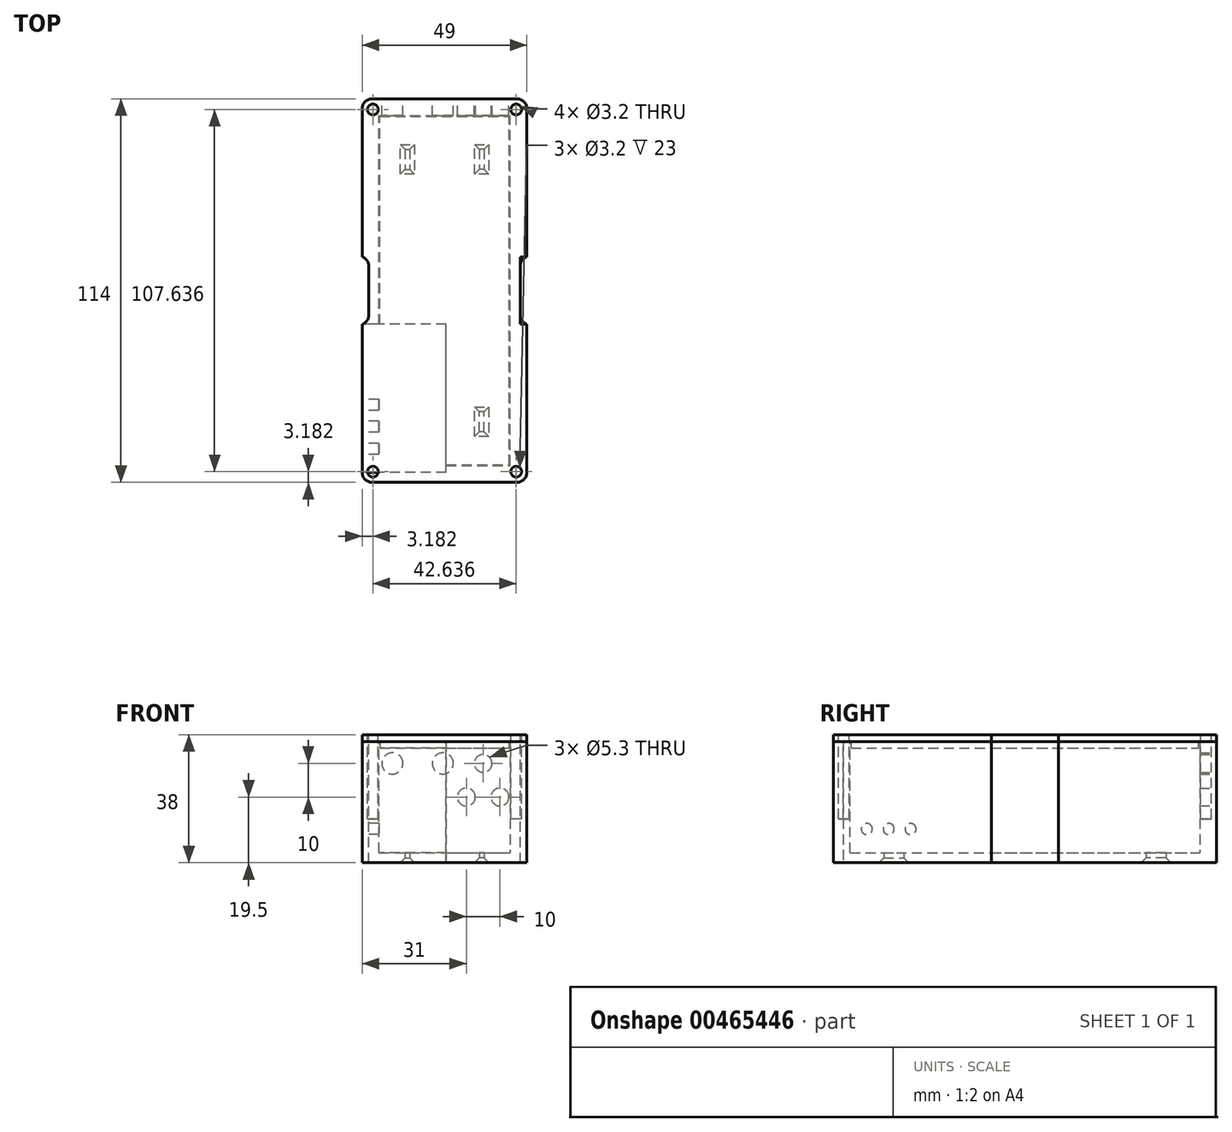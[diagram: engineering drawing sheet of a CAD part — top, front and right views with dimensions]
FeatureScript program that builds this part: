
annotation { "Feature Type Name" : "Feature", "Feature Type Description" : "" }
export const myFeature = defineFeature(function(context is Context, id is Id, definition is map)
    precondition{}
    {
        {
            var Q0;
            Q0=qCreatedBy(makeId("Top.planeOp"),FACE);
            var sketch = newSketch(context, id + "F0", { "sketchPlane" : qUnion([Q0])});
            skLineSegment(sketch, "E0.bottom", {"start": v(0, 0) * mm, "end": v(35, 0) * mm, "construction": true});
            skLineSegment(sketch, "E0.top", {"start": v(0, 100) * mm, "end": v(35, 100) * mm, "construction": true});
            skLineSegment(sketch, "E0.left", {"start": v(0, 0) * mm, "end": v(0, 100) * mm, "construction": true});
            skLineSegment(sketch, "E0.right", {"start": v(35, 0) * mm, "end": v(35, 100) * mm, "construction": true});
            skLineSegment(sketch, "E1.0", {"start": v(37, -2) * mm, "end": v(37, 102) * mm});
            skLineSegment(sketch, "E1.1", {"start": v(-2, -2) * mm, "end": v(37, -2) * mm});
            skLineSegment(sketch, "E1.2", {"start": v(-2, -2) * mm, "end": v(-2, 102) * mm});
            skLineSegment(sketch, "E1.3", {"start": v(-2, 102) * mm, "end": v(37, 102) * mm});
            skLineSegment(sketch, "E2.0", {"start": v(-7, 107) * mm, "end": v(42, 107) * mm});
            skLineSegment(sketch, "E2.1", {"start": v(-7, -7) * mm, "end": v(-7, 107) * mm});
            skLineSegment(sketch, "E2.2", {"start": v(-7, -7) * mm, "end": v(42, -7) * mm});
            skLineSegment(sketch, "E2.3", {"start": v(42, -7) * mm, "end": v(42, 107) * mm});
            skSolve(sketch);
        }
        {
            var Q0;
            Q0 = qSketchRegion(id + "F0", true);
            extrude(context, id + "F1", {"entities" : qUnion([Q0]), "depth" : 33 * mm});
        }
        {
            var Q0;
            Q0=makeQuery(id+"F1.opExtrude","CAP_FACE",FACE,{"disambiguationData":[OSD([sQuery(id+"F0.wireOp",EDGE,"E1.0"),sQuery(id+"F0.wireOp",EDGE,"E1.1"),sQuery(id+"F0.wireOp",EDGE,"E1.2"),sQuery(id+"F0.wireOp",EDGE,"E1.3"),sQuery(id+"F0.wireOp",EDGE,"E2.0"),sQuery(id+"F0.wireOp",EDGE,"E2.1"),sQuery(id+"F0.wireOp",EDGE,"E2.2"),sQuery(id+"F0.wireOp",EDGE,"E2.3")])],"isStart":true});
            var sketch = newSketch(context, id + "F2", { "sketchPlane" : qUnion([Q0])});
            skLineSegment(sketch, "E3.bottom", {"start": v(-7, 7) * mm, "end": v(42, 7) * mm});
            skLineSegment(sketch, "E3.top", {"start": v(-7, -107) * mm, "end": v(42, -107) * mm});
            skLineSegment(sketch, "E3.left", {"start": v(-7, 7) * mm, "end": v(-7, -107) * mm});
            skLineSegment(sketch, "E3.right", {"start": v(42, 7) * mm, "end": v(42, -107) * mm});
            skSolve(sketch);
        }
        {
            var Q0;
            Q0 = qSketchRegion(id + "F2", true);
            extrude(context, id + "F3", {"entities" : qUnion([Q0]), "operationType" : NewBodyOperationType.ADD, "depth" : 3 * mm});
        }
        {
            var Q0;
            Q0=makeQuery(id+"F1.opExtrude","CAP_FACE",FACE,{"disambiguationData":[OSD([sQuery(id+"F0.wireOp",EDGE,"E1.0"),sQuery(id+"F0.wireOp",EDGE,"E1.1"),sQuery(id+"F0.wireOp",EDGE,"E1.2"),sQuery(id+"F0.wireOp",EDGE,"E1.3"),sQuery(id+"F0.wireOp",EDGE,"E2.0"),sQuery(id+"F0.wireOp",EDGE,"E2.1"),sQuery(id+"F0.wireOp",EDGE,"E2.2"),sQuery(id+"F0.wireOp",EDGE,"E2.3")])],"isStart":false});
            var sketch = newSketch(context, id + "F4", { "sketchPlane" : qUnion([Q0])});
            skLineSegment(sketch, "E4.bottom", {"start": v(42, -7) * mm, "end": v(-7, -7) * mm});
            skLineSegment(sketch, "E4.top", {"start": v(42, 107) * mm, "end": v(-7, 107) * mm});
            skLineSegment(sketch, "E4.left", {"start": v(42, -7) * mm, "end": v(42, 107) * mm});
            skLineSegment(sketch, "E4.right", {"start": v(-7, -7) * mm, "end": v(-7, 107) * mm});
            skSolve(sketch);
        }
        {
            var Q0;
            Q0 = qSketchRegion(id + "F4", true);
            extrude(context, id + "F5", {"entities" : qUnion([Q0]), "depth" : 2 * mm});
        }
        {
            var Q0;
            Q0=makeQuery(id+"F5.opExtrude","CAP_FACE",FACE,{"disambiguationData":[OSD([sQuery(id+"F4.wireOp",EDGE,"E4.bottom"),sQuery(id+"F4.wireOp",EDGE,"E4.top"),sQuery(id+"F4.wireOp",EDGE,"E4.left"),sQuery(id+"F4.wireOp",EDGE,"E4.right")])],"isStart":true});
            var sketch = newSketch(context, id + "F6", { "sketchPlane" : qUnion([Q0])});
            skLineSegment(sketch, "E5.0", {"start": v(-2, 2) * mm, "end": v(37, 2) * mm, "construction": true});
            skLineSegment(sketch, "E6.0", {"start": v(37, 2) * mm, "end": v(37, -102) * mm, "construction": true});
            skLineSegment(sketch, "E7.0", {"start": v(-2, -102) * mm, "end": v(37, -102) * mm, "construction": true});
            skLineSegment(sketch, "E8.0", {"start": v(-2, 2) * mm, "end": v(-2, -102) * mm, "construction": true});
            skLineSegment(sketch, "E9.0", {"start": v(-1.7, 1.7) * mm, "end": v(36.7, 1.7) * mm});
            skLineSegment(sketch, "E9.1", {"start": v(-1.7, 1.7) * mm, "end": v(-1.7, -101.7) * mm});
            skLineSegment(sketch, "E9.2", {"start": v(-1.7, -101.7) * mm, "end": v(36.7, -101.7) * mm});
            skLineSegment(sketch, "E9.3", {"start": v(36.7, 1.7) * mm, "end": v(36.7, -101.7) * mm});
            skSolve(sketch);
        }
        {
            var Q0;
            Q0 = qSketchRegion(id + "F6", true);
            extrude(context, id + "F7", {"entities" : qUnion([Q0]), "operationType" : NewBodyOperationType.ADD, "depth" : 2 * mm});
        }
        {
            var Q0;
            Q0=makeQuery(id+"F5.opExtrude","CAP_FACE",FACE,{"disambiguationData":[OSD([sQuery(id+"F4.wireOp",EDGE,"E4.bottom"),sQuery(id+"F4.wireOp",EDGE,"E4.top"),sQuery(id+"F4.wireOp",EDGE,"E4.left"),sQuery(id+"F4.wireOp",EDGE,"E4.right")])],"isStart":false});
            var sketch = newSketch(context, id + "F8", { "sketchPlane" : qUnion([Q0])});
            skCircle(sketch, "E10", {"center": v(-3.82, -3.82) * mm, "radius": 1.3 * mm});
            skLineSegment(sketch, "E11", {"start": v(-2, -2) * mm, "end": v(-7, -7) * mm});
            skLineSegment(sketch, "E12", {"start": v(17.5, -7) * mm, "end": v(17.5, -36.45) * mm, "construction": true});
            skLineSegment(sketch, "E13", {"start": v(-7, 50) * mm, "end": v(-34.4, 50) * mm, "construction": true});
            skCircle(sketch, "E14.MirrorC", {"center": v(-3.82, 103.82) * mm, "radius": 1.3 * mm});
            skCircle(sketch, "E15.MirrorC", {"center": v(38.82, 103.82) * mm, "radius": 1.3 * mm});
            skCircle(sketch, "E16.MirrorC", {"center": v(38.82, -3.82) * mm, "radius": 1.3 * mm});
            skSolve(sketch);
        }
        {
            var Q0;
            Q0 = qSketchRegion(id + "F8", true);
            extrude(context, id + "F9", {"entities" : qUnion([Q0]), "operationType" : NewBodyOperationType.REMOVE, "oppositeDirection" : true, "depth" : 25 * mm});
        }
        {
            var Q0;
            Q0=makeQuery(id+"F5.opExtrude","CAP_FACE",FACE,{"disambiguationData":[OSD([sQuery(id+"F4.wireOp",EDGE,"E4.bottom"),sQuery(id+"F4.wireOp",EDGE,"E4.top"),sQuery(id+"F4.wireOp",EDGE,"E4.left"),sQuery(id+"F4.wireOp",EDGE,"E4.right")])],"isStart":false});
            var sketch = newSketch(context, id + "F10", { "sketchPlane" : qUnion([Q0])});
            skCircle(sketch, "E17", {"center": v(-3.82, -3.82) * mm, "radius": 1.6 * mm});
            skCircle(sketch, "E18.MirrorC", {"center": v(-3.82, 103.82) * mm, "radius": 1.6 * mm});
            skCircle(sketch, "E19.MirrorC", {"center": v(38.82, -3.82) * mm, "radius": 1.6 * mm});
            skCircle(sketch, "E20.MirrorC", {"center": v(38.82, 103.82) * mm, "radius": 1.6 * mm});
            skSolve(sketch);
        }
        {
            var Q0;
            Q0 = qSketchRegion(id + "F10", true);
            extrude(context, id + "F11", {"entities" : qUnion([Q0]), "operationType" : NewBodyOperationType.REMOVE, "oppositeDirection" : true, "depth" : 25 * mm});
        }
        {
            var Q0;
            Q0=makeQuery(id+"F8.imprint","IMPRINT",FACE,{"disambiguationData":[TD([[makeQuery(id+"F8.imprint","IMPRINT",EDGE,{"derivedFrom":sQuery(id+"F8.wireOp",EDGE,"E14.MirrorC")}),1.0]])]});
            var sketch = newSketch(context, id + "F12", { "sketchPlane" : qUnion([Q0])});
            skLineSegment(sketch, "E21.bottom", {"start": v(-7, 60) * mm, "end": v(-5, 60) * mm});
            skLineSegment(sketch, "E21.top", {"start": v(-7, 40) * mm, "end": v(-5, 40) * mm});
            skLineSegment(sketch, "E21.left", {"start": v(-7, 60) * mm, "end": v(-7, 40) * mm});
            skLineSegment(sketch, "E21.right", {"start": v(-5, 60) * mm, "end": v(-5, 40) * mm});
            skPoint(sketch, "E22", {"position": v(-7, 50) * mm});
            skLineSegment(sketch, "E23.MirrorCS", {"start": v(42, 60) * mm, "end": v(42, 40) * mm});
            skLineSegment(sketch, "E24.MirrorCS", {"start": v(42, 60) * mm, "end": v(40, 60) * mm});
            skLineSegment(sketch, "E25.MirrorCS", {"start": v(40, 60) * mm, "end": v(40, 40) * mm});
            skLineSegment(sketch, "E26.MirrorCS", {"start": v(42, 40) * mm, "end": v(40, 40) * mm});
            skSolve(sketch);
        }
        {
            var Q0;
            Q0 = qSketchRegion(id + "F12", true);
            extrude(context, id + "F13", {"entities" : qUnion([Q0]), "operationType" : NewBodyOperationType.REMOVE, "endBound" : BoundingType.THROUGH_ALL, "oppositeDirection" : true, "depth" : 25 * mm});
        }
        {
            var Q0;
            {var subQ0=sQuery(id+"F12.wireOp",EDGE,"E21.bottom");var subQ1=sQuery(id+"F12.wireOp",EDGE,"E21.right");Q0=makeQuery(id+"F13.boolean.opBoolean","COPY",EDGE,{"disambiguationData":[TD([makeQuery(id+"F3.opExtrude","CAP_FACE",FACE,{"disambiguationData":[OSD([sQuery(id+"F2.wireOp",EDGE,"E3.bottom"),sQuery(id+"F2.wireOp",EDGE,"E3.top"),sQuery(id+"F2.wireOp",EDGE,"E3.left"),sQuery(id+"F2.wireOp",EDGE,"E3.right")])],"isStart":false})])],"derivedFrom":makeQuery(id+"F13.opExtrude","SWEPT_EDGE",EDGE,{"disambiguationData":[OSD([subQ0,subQ1])]})});}
            var Q1;
            {var subQ0=sQuery(id+"F4.wireOp",EDGE,"E4.right");var subQ1=sQuery(id+"F4.wireOp",EDGE,"E4.left");var subQ2=sQuery(id+"F4.wireOp",EDGE,"E4.top");var subQ3=sQuery(id+"F4.wireOp",EDGE,"E4.bottom");var subQ4=sQuery(id+"F12.wireOp",EDGE,"E21.bottom");var subQ5=sQuery(id+"F12.wireOp",EDGE,"E21.right");Q1=makeQuery(id+"F13.boolean.opBoolean","COPY",EDGE,{"disambiguationData":[TD([makeQuery(id+"F5.opExtrude","CAP_FACE",FACE,{"disambiguationData":[OSD([subQ3,subQ2,subQ1,subQ0])],"isStart":true})])],"derivedFrom":makeQuery(id+"F13.opExtrude","SWEPT_EDGE",EDGE,{"disambiguationData":[OSD([subQ4,subQ5])]})});}
            var Q2;
            {var subQ0=sQuery(id+"F4.wireOp",EDGE,"E4.right");var subQ1=sQuery(id+"F4.wireOp",EDGE,"E4.left");var subQ2=sQuery(id+"F4.wireOp",EDGE,"E4.top");var subQ3=sQuery(id+"F4.wireOp",EDGE,"E4.bottom");var subQ4=sQuery(id+"F12.wireOp",EDGE,"E21.top");var subQ5=sQuery(id+"F12.wireOp",EDGE,"E21.right");Q2=makeQuery(id+"F13.boolean.opBoolean","COPY",EDGE,{"disambiguationData":[TD([makeQuery(id+"F5.opExtrude","CAP_FACE",FACE,{"disambiguationData":[OSD([subQ3,subQ2,subQ1,subQ0])],"isStart":true})])],"derivedFrom":makeQuery(id+"F13.opExtrude","SWEPT_EDGE",EDGE,{"disambiguationData":[OSD([subQ4,subQ5])]})});}
            var Q3;
            {var subQ0=sQuery(id+"F12.wireOp",EDGE,"E21.right");var subQ1=sQuery(id+"F12.wireOp",EDGE,"E21.top");Q3=makeQuery(id+"F13.boolean.opBoolean","COPY",EDGE,{"disambiguationData":[TD([makeQuery(id+"F3.opExtrude","CAP_FACE",FACE,{"disambiguationData":[OSD([sQuery(id+"F2.wireOp",EDGE,"E3.bottom"),sQuery(id+"F2.wireOp",EDGE,"E3.top"),sQuery(id+"F2.wireOp",EDGE,"E3.left"),sQuery(id+"F2.wireOp",EDGE,"E3.right")])],"isStart":false})])],"derivedFrom":makeQuery(id+"F13.opExtrude","SWEPT_EDGE",EDGE,{"disambiguationData":[OSD([subQ1,subQ0])]})});}
            var Q4;
            {var subQ0=sQuery(id+"F12.wireOp",EDGE,"E25.MirrorCS");var subQ1=sQuery(id+"F12.wireOp",EDGE,"E24.MirrorCS");Q4=makeQuery(id+"F13.boolean.opBoolean","COPY",EDGE,{"disambiguationData":[TD([makeQuery(id+"F3.opExtrude","CAP_FACE",FACE,{"disambiguationData":[OSD([sQuery(id+"F2.wireOp",EDGE,"E3.bottom"),sQuery(id+"F2.wireOp",EDGE,"E3.top"),sQuery(id+"F2.wireOp",EDGE,"E3.left"),sQuery(id+"F2.wireOp",EDGE,"E3.right")])],"isStart":false})])],"derivedFrom":makeQuery(id+"F13.opExtrude","SWEPT_EDGE",EDGE,{"disambiguationData":[OSD([subQ1,subQ0])]})});}
            var Q5;
            {var subQ0=sQuery(id+"F12.wireOp",EDGE,"E25.MirrorCS");var subQ1=sQuery(id+"F12.wireOp",EDGE,"E26.MirrorCS");Q5=makeQuery(id+"F13.boolean.opBoolean","COPY",EDGE,{"disambiguationData":[TD([makeQuery(id+"F3.opExtrude","CAP_FACE",FACE,{"disambiguationData":[OSD([sQuery(id+"F2.wireOp",EDGE,"E3.bottom"),sQuery(id+"F2.wireOp",EDGE,"E3.top"),sQuery(id+"F2.wireOp",EDGE,"E3.left"),sQuery(id+"F2.wireOp",EDGE,"E3.right")])],"isStart":false})])],"derivedFrom":makeQuery(id+"F13.opExtrude","SWEPT_EDGE",EDGE,{"disambiguationData":[OSD([subQ0,subQ1])]})});}
            var Q6;
            Q6=makeQuery(id+"F3.boolean.opBoolean","MERGE",EDGE,{"derivedFrom":[makeQuery(id+"F1.opExtrude","SWEPT_EDGE",EDGE,{"disambiguationData":[OSD([sQuery(id+"F0.wireOp",EDGE,"E2.0"),sQuery(id+"F0.wireOp",EDGE,"E2.1")])]}),makeQuery(id+"F3.opExtrude","SWEPT_EDGE",EDGE,{"disambiguationData":[OSD([sQuery(id+"F2.wireOp",EDGE,"E3.top"),sQuery(id+"F2.wireOp",EDGE,"E3.left")])]})]});
            var Q7;
            Q7=makeQuery(id+"F3.boolean.opBoolean","MERGE",EDGE,{"derivedFrom":[makeQuery(id+"F1.opExtrude","SWEPT_EDGE",EDGE,{"disambiguationData":[OSD([sQuery(id+"F0.wireOp",EDGE,"E2.0"),sQuery(id+"F0.wireOp",EDGE,"E2.3")])]}),makeQuery(id+"F3.opExtrude","SWEPT_EDGE",EDGE,{"disambiguationData":[OSD([sQuery(id+"F2.wireOp",EDGE,"E3.top"),sQuery(id+"F2.wireOp",EDGE,"E3.right")])]})]});
            var Q8;
            Q8=makeQuery(id+"F5.opExtrude","SWEPT_EDGE",EDGE,{"disambiguationData":[OSD([sQuery(id+"F4.wireOp",EDGE,"E4.top"),sQuery(id+"F4.wireOp",EDGE,"E4.left")])]});
            var Q9;
            Q9=makeQuery(id+"F5.opExtrude","SWEPT_EDGE",EDGE,{"disambiguationData":[OSD([sQuery(id+"F4.wireOp",EDGE,"E4.top"),sQuery(id+"F4.wireOp",EDGE,"E4.right")])]});
            var Q10;
            Q10=makeQuery(id+"F3.boolean.opBoolean","MERGE",EDGE,{"derivedFrom":[makeQuery(id+"F1.opExtrude","SWEPT_EDGE",EDGE,{"disambiguationData":[OSD([sQuery(id+"F0.wireOp",EDGE,"E2.1"),sQuery(id+"F0.wireOp",EDGE,"E2.2")])]}),makeQuery(id+"F3.opExtrude","SWEPT_EDGE",EDGE,{"disambiguationData":[OSD([sQuery(id+"F2.wireOp",EDGE,"E3.bottom"),sQuery(id+"F2.wireOp",EDGE,"E3.left")])]})]});
            var Q11;
            Q11=makeQuery(id+"F5.opExtrude","SWEPT_EDGE",EDGE,{"disambiguationData":[OSD([sQuery(id+"F4.wireOp",EDGE,"E4.bottom"),sQuery(id+"F4.wireOp",EDGE,"E4.right")])]});
            var Q12;
            Q12=makeQuery(id+"F5.opExtrude","SWEPT_EDGE",EDGE,{"disambiguationData":[OSD([sQuery(id+"F4.wireOp",EDGE,"E4.bottom"),sQuery(id+"F4.wireOp",EDGE,"E4.left")])]});
            var Q13;
            Q13=makeQuery(id+"F3.boolean.opBoolean","MERGE",EDGE,{"derivedFrom":[makeQuery(id+"F1.opExtrude","SWEPT_EDGE",EDGE,{"disambiguationData":[OSD([sQuery(id+"F0.wireOp",EDGE,"E2.2"),sQuery(id+"F0.wireOp",EDGE,"E2.3")])]}),makeQuery(id+"F3.opExtrude","SWEPT_EDGE",EDGE,{"disambiguationData":[OSD([sQuery(id+"F2.wireOp",EDGE,"E3.bottom"),sQuery(id+"F2.wireOp",EDGE,"E3.right")])]})]});
            fillet(context, id + "F14", {"entities" : qUnion([Q0, Q1, Q2, Q3, Q4, Q5, Q6, Q7, Q8, Q9, Q10, Q11, Q12, Q13]), "radius" : 3 * mm, "tangentPropagation" : true, "allowEdgeOverflow" : false});
        }
        {
            var Q0;
            Q0=makeQuery(id+"F3.boolean.opBoolean","MERGE",FACE,{"derivedFrom":[makeQuery(id+"F1.opExtrude","SWEPT_FACE",FACE,{"disambiguationData":[OSD([sQuery(id+"F0.wireOp",EDGE,"E2.0")])]}),makeQuery(id+"F3.opExtrude","SWEPT_FACE",FACE,{"disambiguationData":[OSD([sQuery(id+"F2.wireOp",EDGE,"E3.top")])]})]});
            var sketch = newSketch(context, id + "F15", { "sketchPlane" : qUnion([Q0])});
            skCircle(sketch, "E27", {"center": v(-17, 26.5) * mm, "radius": 3.15 * mm});
            skLineSegment(sketch, "E28", {"start": v(-2, 26.5) * mm, "end": v(-23.16, 26.5) * mm, "construction": true});
            skCircle(sketch, "E29", {"center": v(-2, 26.5) * mm, "radius": 3.15 * mm});
            skSolve(sketch);
        }
        {
            var Q0;
            Q0 = qSketchRegion(id + "F15", true);
            extrude(context, id + "F16", {"entities" : qUnion([Q0]), "operationType" : NewBodyOperationType.REMOVE, "oppositeDirection" : true, "depth" : 25 * mm});
        }
        {
            var Q0;
            Q0=makeQuery(id+"F3.opExtrude","CAP_FACE",FACE,{"disambiguationData":[OSD([sQuery(id+"F2.wireOp",EDGE,"E3.bottom"),sQuery(id+"F2.wireOp",EDGE,"E3.top"),sQuery(id+"F2.wireOp",EDGE,"E3.left"),sQuery(id+"F2.wireOp",EDGE,"E3.right")])],"isStart":false});
            var sketch = newSketch(context, id + "F17", { "sketchPlane" : qUnion([Q0])});
            skLineSegment(sketch, "E30.bottom", {"start": v(11.2, 21.25) * mm, "end": v(23.8, 21.25) * mm});
            skLineSegment(sketch, "E30.top", {"start": v(11.2, -119.18) * mm, "end": v(23.8, -119.18) * mm});
            skLineSegment(sketch, "E30.left", {"start": v(11.2, 21.25) * mm, "end": v(11.2, -119.18) * mm, "construction": true});
            skLineSegment(sketch, "E30.right", {"start": v(23.8, 21.25) * mm, "end": v(23.8, -119.18) * mm, "construction": true});
            skPoint(sketch, "E31", {"position": v(17.5, 21.25) * mm});
            skLineSegment(sketch, "E32.bottom", {"start": v(5.7, -8) * mm, "end": v(7.2, -8) * mm});
            skLineSegment(sketch, "E32.top", {"start": v(5.7, -14) * mm, "end": v(7.2, -14) * mm});
            skLineSegment(sketch, "E32.left", {"start": v(5.7, -8) * mm, "end": v(5.7, -14) * mm});
            skLineSegment(sketch, "E32.right", {"start": v(7.2, -8) * mm, "end": v(7.2, -14) * mm});
            skLineSegment(sketch, "E33.MirrorCS", {"start": v(29.3, -8) * mm, "end": v(27.8, -8) * mm});
            skLineSegment(sketch, "E34.MirrorCS", {"start": v(29.3, -14) * mm, "end": v(27.8, -14) * mm});
            skLineSegment(sketch, "E35.MirrorCS", {"start": v(29.3, -8) * mm, "end": v(29.3, -14) * mm});
            skLineSegment(sketch, "E36.MirrorCS", {"start": v(27.8, -8) * mm, "end": v(27.8, -14) * mm});
            skLineSegment(sketch, "E37.MirrorCS", {"start": v(29.3, -86) * mm, "end": v(27.8, -86) * mm});
            skLineSegment(sketch, "E38.MirrorCS", {"start": v(5.7, -92) * mm, "end": v(7.2, -92) * mm});
            skLineSegment(sketch, "E39.MirrorCS", {"start": v(5.7, -86) * mm, "end": v(7.2, -86) * mm});
            skLineSegment(sketch, "E40.MirrorCS", {"start": v(29.3, -92) * mm, "end": v(27.8, -92) * mm});
            skLineSegment(sketch, "E41.MirrorCS", {"start": v(27.8, -92) * mm, "end": v(27.8, -86) * mm});
            skLineSegment(sketch, "E42.MirrorCS", {"start": v(29.3, -92) * mm, "end": v(29.3, -86) * mm});
            skLineSegment(sketch, "E43.MirrorCS", {"start": v(7.2, -92) * mm, "end": v(7.2, -86) * mm});
            skLineSegment(sketch, "E44.MirrorCS", {"start": v(5.7, -92) * mm, "end": v(5.7, -86) * mm});
            skSolve(sketch);
        }
        {
            var Q0;
            Q0 = qSketchRegion(id + "F17", true);
            extrude(context, id + "F18", {"entities" : qUnion([Q0]), "operationType" : NewBodyOperationType.REMOVE, "oppositeDirection" : true, "depth" : 25 * mm});
        }
        {
            var Q0;
            Q0=makeQuery(id+"F3.opExtrude","CAP_FACE",FACE,{"disambiguationData":[OSD([sQuery(id+"F2.wireOp",EDGE,"E3.bottom"),sQuery(id+"F2.wireOp",EDGE,"E3.top"),sQuery(id+"F2.wireOp",EDGE,"E3.left"),sQuery(id+"F2.wireOp",EDGE,"E3.right")])],"isStart":false});
            var sketch = newSketch(context, id + "F19", { "sketchPlane" : qUnion([Q0])});
            skLineSegment(sketch, "E45.0", {"start": v(8.6, -6.6) * mm, "end": v(8.6, -15.4) * mm});
            skLineSegment(sketch, "E45.1", {"start": v(4.3, -6.6) * mm, "end": v(8.6, -6.6) * mm});
            skLineSegment(sketch, "E45.2", {"start": v(4.3, -6.6) * mm, "end": v(4.3, -15.4) * mm});
            skLineSegment(sketch, "E45.3", {"start": v(4.3, -15.4) * mm, "end": v(8.6, -15.4) * mm});
            skLineSegment(sketch, "E46.MirrorCS", {"start": v(30.7, -6.6) * mm, "end": v(26.4, -6.6) * mm});
            skLineSegment(sketch, "E47.MirrorCS", {"start": v(26.4, -6.6) * mm, "end": v(26.4, -15.4) * mm});
            skLineSegment(sketch, "E48.MirrorCS", {"start": v(30.7, -6.6) * mm, "end": v(30.7, -15.4) * mm});
            skLineSegment(sketch, "E49.MirrorCS", {"start": v(30.7, -15.4) * mm, "end": v(26.4, -15.4) * mm});
            skLineSegment(sketch, "E50.MirrorCS", {"start": v(4.3, -93.4) * mm, "end": v(8.6, -93.4) * mm});
            skLineSegment(sketch, "E51.MirrorCS", {"start": v(8.6, -93.4) * mm, "end": v(8.6, -84.6) * mm});
            skLineSegment(sketch, "E52.MirrorCS", {"start": v(4.3, -93.4) * mm, "end": v(4.3, -84.6) * mm});
            skLineSegment(sketch, "E53.MirrorCS", {"start": v(4.3, -84.6) * mm, "end": v(8.6, -84.6) * mm});
            skLineSegment(sketch, "E54.MirrorCS", {"start": v(30.7, -93.4) * mm, "end": v(26.4, -93.4) * mm});
            skLineSegment(sketch, "E55.MirrorCS", {"start": v(26.4, -93.4) * mm, "end": v(26.4, -84.6) * mm});
            skLineSegment(sketch, "E56.MirrorCS", {"start": v(30.7, -84.6) * mm, "end": v(26.4, -84.6) * mm});
            skLineSegment(sketch, "E57.MirrorCS", {"start": v(30.7, -93.4) * mm, "end": v(30.7, -84.6) * mm});
            skSolve(sketch);
        }
        {
            var Q0;
            Q0 = qSketchRegion(id + "F19", true);
            extrude(context, id + "F20", {"entities" : qUnion([Q0]), "operationType" : NewBodyOperationType.REMOVE, "oppositeDirection" : true, "depth" : 25 * mm, "hasDraft" : true, "draftAngle" : 45 * degree, "draftPullDirection" : true});
        }
        {
            var Q0;
            Q0=makeQuery(id+"F3.boolean.opBoolean","MERGE",FACE,{"derivedFrom":[makeQuery(id+"F1.opExtrude","SWEPT_FACE",FACE,{"disambiguationData":[OSD([sQuery(id+"F0.wireOp",EDGE,"E2.0")])]}),makeQuery(id+"F3.opExtrude","SWEPT_FACE",FACE,{"disambiguationData":[OSD([sQuery(id+"F2.wireOp",EDGE,"E3.top")])]})]});
            var sketch = newSketch(context, id + "F21", { "sketchPlane" : qUnion([Q0])});
            skCircle(sketch, "E58", {"center": v(-34, 16.5) * mm, "radius": 2.65 * mm});
            skLineSegment(sketch, "E59", {"start": v(-34, 16.5) * mm, "end": v(-24, 16.5) * mm, "construction": true});
            skCircle(sketch, "E60", {"center": v(-24, 16.5) * mm, "radius": 2.65 * mm});
            skLineSegment(sketch, "E61", {"start": v(-29, 16.5) * mm, "end": v(-29, 26.5) * mm, "construction": true});
            skCircle(sketch, "E62", {"center": v(-29, 26.5) * mm, "radius": 2.65 * mm});
            skLineSegment(sketch, "E63", {"start": v(-17, 26.5) * mm, "end": v(-33.32, 26.5) * mm, "construction": true});
            skSolve(sketch);
        }
        {
            var Q0;
            Q0 = qSketchRegion(id + "F21", true);
            extrude(context, id + "F22", {"entities" : qUnion([Q0]), "operationType" : NewBodyOperationType.REMOVE, "oppositeDirection" : true, "depth" : 25 * mm});
        }
        {
            var Q0;
            {var subQ0=sQuery(id+"F2.wireOp",EDGE,"E3.left");var subQ2=sQuery(id+"F0.wireOp",EDGE,"E2.2");var subQ3=sQuery(id+"F0.wireOp",EDGE,"E2.1");Q0=makeQuery(id+"F13.boolean.opBoolean","SPLIT",FACE,{"disambiguationData":[TD([makeQuery(id+"F1.opExtrude","SWEPT_FACE",FACE,{"disambiguationData":[OSD([subQ2])]})])],"derivedFrom":makeQuery(id+"F3.boolean.opBoolean","MERGE",FACE,{"derivedFrom":[makeQuery(id+"F1.opExtrude","SWEPT_FACE",FACE,{"disambiguationData":[OSD([subQ3])]}),makeQuery(id+"F3.opExtrude","SWEPT_FACE",FACE,{"disambiguationData":[OSD([subQ0])]})]})});}
            var sketch = newSketch(context, id + "F23", { "sketchPlane" : qUnion([Q0])});
            skCircle(sketch, "E64", {"center": v(-3, 23) * mm, "radius": 1.65 * mm});
            skCircle(sketch, "E65.1.0.0", {"center": v(-9.5, 23) * mm, "radius": 1.65 * mm});
            skCircle(sketch, "E65.2.0.0", {"center": v(-16, 23) * mm, "radius": 1.65 * mm});
            skLineSegment(sketch, "E65.direction1", {"start": v(-3, 23) * mm, "end": v(-9.5, 23) * mm, "construction": true});
            skLineSegment(sketch, "E66", {"start": v(7, 15) * mm, "end": v(-67.8, 15) * mm, "construction": true});
            skPoint(sketch, "E67", {"position": v(7, 15) * mm});
            skLineSegment(sketch, "E68.MirrorCS", {"start": v(-3, 7) * mm, "end": v(-9.5, 7) * mm, "construction": true});
            skCircle(sketch, "E69.MirrorC", {"center": v(-9.5, 7) * mm, "radius": 1.65 * mm});
            skCircle(sketch, "E70.MirrorC", {"center": v(-16, 7) * mm, "radius": 1.65 * mm});
            skCircle(sketch, "E71.MirrorC", {"center": v(-3, 7) * mm, "radius": 1.65 * mm});
            skSolve(sketch);
        }
        {
            var Q0;
            Q0=makeQuery(id+"F23.imprint","IMPRINT",FACE,{"disambiguationData":[TD([[makeQuery(id+"F23.imprint","IMPRINT",EDGE,{"derivedFrom":sQuery(id+"F23.wireOp",EDGE,"E65.1.0.0")}),1.0]])]});
            var Q1;
            Q1=makeQuery(id+"F23.imprint","IMPRINT",FACE,{"disambiguationData":[TD([[makeQuery(id+"F23.imprint","IMPRINT",EDGE,{"derivedFrom":sQuery(id+"F23.wireOp",EDGE,"E65.2.0.0")}),1.0]])]});
            var Q2;
            Q2=makeQuery(id+"F23.imprint","IMPRINT",FACE,{"disambiguationData":[TD([[makeQuery(id+"F23.imprint","IMPRINT",EDGE,{"derivedFrom":sQuery(id+"F23.wireOp",EDGE,"E64")}),1.0]])]});
            var Q3;
            Q3=makeQuery(id+"F23.imprint","IMPRINT",FACE,{"disambiguationData":[TD([[makeQuery(id+"F23.imprint","IMPRINT",EDGE,{"derivedFrom":sQuery(id+"F23.wireOp",EDGE,"E71.MirrorC")}),-1.0]])]});
            var Q4;
            Q4=makeQuery(id+"F23.imprint","IMPRINT",FACE,{"disambiguationData":[TD([[makeQuery(id+"F23.imprint","IMPRINT",EDGE,{"derivedFrom":sQuery(id+"F23.wireOp",EDGE,"E69.MirrorC")}),-1.0]])]});
            var Q5;
            Q5=makeQuery(id+"F23.imprint","IMPRINT",FACE,{"disambiguationData":[TD([[makeQuery(id+"F23.imprint","IMPRINT",EDGE,{"derivedFrom":sQuery(id+"F23.wireOp",EDGE,"E70.MirrorC")}),-1.0]])]});
            extrude(context, id + "F24", {"entities" : qUnion([Q0, Q1, Q2, Q3, Q4, Q5]), "operationType" : NewBodyOperationType.REMOVE, "oppositeDirection" : true, "depth" : 25 * mm});
        }
    });
